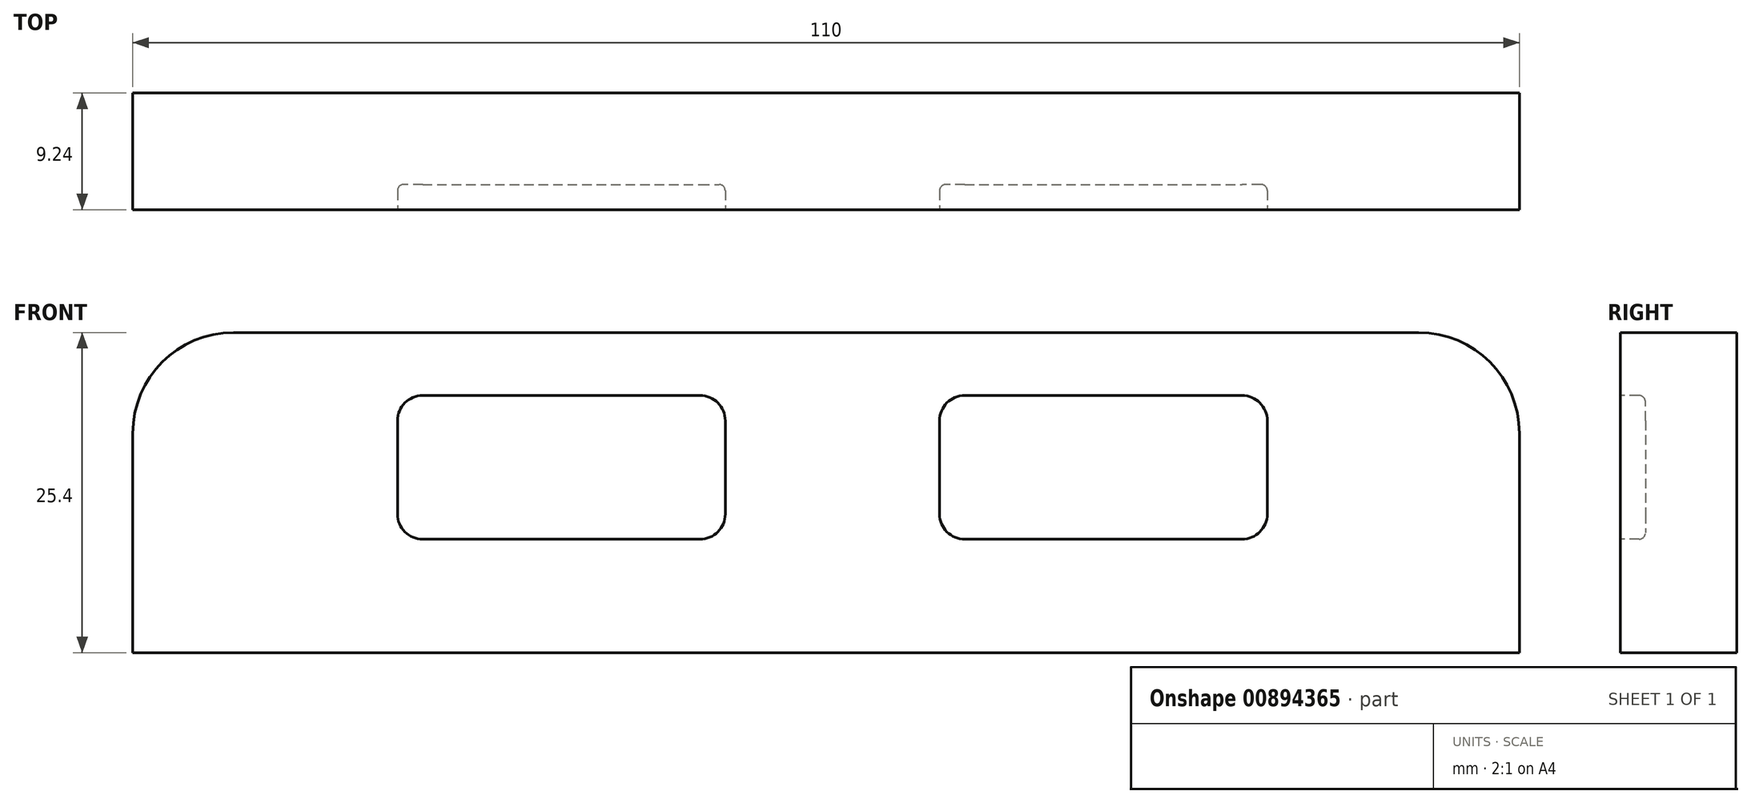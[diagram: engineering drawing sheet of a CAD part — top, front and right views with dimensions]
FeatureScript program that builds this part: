
annotation { "Feature Type Name" : "Feature", "Feature Type Description" : "" }
export const myFeature = defineFeature(function(context is Context, id is Id, definition is map)
    precondition{}
    {
        {
            var Q0;
            Q0=qCreatedBy(makeId("Front.planeOp"),FACE);
            var sketch = newSketch(context, id + "F0", { "sketchPlane" : qUnion([Q0])});
            skLineSegment(sketch, "E0.bottom", {"start": v(-1, 0) * mm, "end": v(109, 0) * mm});
            skLineSegment(sketch, "E0.top", {"start": v(-1, 25.4) * mm, "end": v(109, 25.4) * mm});
            skLineSegment(sketch, "E0.left", {"start": v(-1, 0) * mm, "end": v(-1, 25.4) * mm});
            skLineSegment(sketch, "E0.right", {"start": v(109, 0) * mm, "end": v(109, 25.4) * mm});
            skSolve(sketch);
        }
        {
            var Q0;
            Q0=makeQuery(id+"F0.imprint","IMPRINT",FACE,{"disambiguationData":[TD([[makeQuery(id+"F0.imprint","IMPRINT",EDGE,{"derivedFrom":sQuery(id+"F0.wireOp",EDGE,"E0.bottom")}),1.0]])]});
            extrude(context, id + "F1", {"entities" : qUnion([Q0]), "endBound" : BoundingType.SYMMETRIC, "depth" : 9.25 * mm, "offsetDistance" : 25 * mm});
        }
        {
            var Q0;
            Q0=makeQuery(id+"F1.opExtrude","CAP_FACE",FACE,{"disambiguationData":[OSD([sQuery(id+"F0.wireOp",EDGE,"E0.bottom"),sQuery(id+"F0.wireOp",EDGE,"E0.top"),sQuery(id+"F0.wireOp",EDGE,"E0.left"),sQuery(id+"F0.wireOp",EDGE,"E0.right")])],"isStart":false});
            var sketch = newSketch(context, id + "F2", { "sketchPlane" : qUnion([Q0])});
            skLineSegment(sketch, "E1.bottom", {"start": v(22, 9) * mm, "end": v(44, 9) * mm});
            skLineSegment(sketch, "E1.top", {"start": v(22, 20.4) * mm, "end": v(44, 20.4) * mm});
            skLineSegment(sketch, "E1.left", {"start": v(20, 11) * mm, "end": v(20, 18.4) * mm});
            skLineSegment(sketch, "E1.right", {"start": v(46, 11) * mm, "end": v(46, 18.4) * mm});
            skLineSegment(sketch, "E2.bottom", {"start": v(65, 20.4) * mm, "end": v(87, 20.4) * mm});
            skLineSegment(sketch, "E2.top", {"start": v(65, 9) * mm, "end": v(87, 9) * mm});
            skLineSegment(sketch, "E2.left", {"start": v(63, 18.4) * mm, "end": v(63, 11) * mm});
            skLineSegment(sketch, "E2.right", {"start": v(89, 18.4) * mm, "end": v(89, 11) * mm});
            skPoint(sketch, "E3.visualSharp", {"position": v(20, 20.4) * mm});
            skArc(sketch, "E3.filletArc", {"start": v(22, 20.4) * mm, "mid": v(20.59, 19.81) * mm, "end": v(20, 18.4) * mm});
            skPoint(sketch, "E4.visualSharp", {"position": v(20, 9) * mm});
            skArc(sketch, "E4.filletArc", {"start": v(20, 11) * mm, "mid": v(20.59, 9.59) * mm, "end": v(22, 9) * mm});
            skPoint(sketch, "E5.visualSharp", {"position": v(46, 9) * mm});
            skArc(sketch, "E5.filletArc", {"start": v(44, 9) * mm, "mid": v(45.41, 9.59) * mm, "end": v(46, 11) * mm});
            skPoint(sketch, "E6.visualSharp", {"position": v(46, 20.4) * mm});
            skArc(sketch, "E6.filletArc", {"start": v(46, 18.4) * mm, "mid": v(45.41, 19.81) * mm, "end": v(44, 20.4) * mm});
            skPoint(sketch, "E7.visualSharp", {"position": v(63, 20.4) * mm});
            skArc(sketch, "E7.filletArc", {"start": v(65, 20.4) * mm, "mid": v(63.59, 19.81) * mm, "end": v(63, 18.4) * mm});
            skPoint(sketch, "E8.visualSharp", {"position": v(63, 9) * mm});
            skArc(sketch, "E8.filletArc", {"start": v(63, 11) * mm, "mid": v(63.59, 9.59) * mm, "end": v(65, 9) * mm});
            skPoint(sketch, "E9.visualSharp", {"position": v(89, 9) * mm});
            skArc(sketch, "E9.filletArc", {"start": v(87, 9) * mm, "mid": v(88.41, 9.59) * mm, "end": v(89, 11) * mm});
            skPoint(sketch, "E10.visualSharp", {"position": v(89, 20.4) * mm});
            skArc(sketch, "E10.filletArc", {"start": v(89, 18.4) * mm, "mid": v(88.41, 19.81) * mm, "end": v(87, 20.4) * mm});
            skSolve(sketch);
        }
        {
            var Q0;
            Q0 = qSketchRegion(id + "F2", true);
            extrude(context, id + "F3", {"entities" : qUnion([Q0]), "operationType" : NewBodyOperationType.REMOVE, "oppositeDirection" : true, "depth" : 2 * mm, "offsetDistance" : 25 * mm});
        }
        {
            var Q0;
            Q0=makeQuery(id+"F3.boolean.opBoolean","COPY",EDGE,{"derivedFrom":makeQuery(id+"F3.opExtrude","CAP_EDGE",EDGE,{"disambiguationData":[OSD([sQuery(id+"F2.wireOp",EDGE,"E2.right")])],"isStart":false})});
            var Q1;
            Q1=makeQuery(id+"F3.boolean.opBoolean","COPY",EDGE,{"derivedFrom":makeQuery(id+"F3.opExtrude","CAP_EDGE",EDGE,{"disambiguationData":[OSD([sQuery(id+"F2.wireOp",EDGE,"E1.right")])],"isStart":false})});
            fillet(context, id + "F4", {"entities" : qUnion([Q0, Q1]), "radius" : .5 * mm, "tangentPropagation" : true, "allowEdgeOverflow" : false});
        }
        {
            var Q0;
            Q0=makeQuery(id+"F1.opExtrude","SWEPT_EDGE",EDGE,{"disambiguationData":[OSD([sQuery(id+"F0.wireOp",EDGE,"E0.top"),sQuery(id+"F0.wireOp",EDGE,"E0.right")])]});
            var Q1;
            Q1=makeQuery(id+"F1.opExtrude","SWEPT_EDGE",EDGE,{"disambiguationData":[OSD([sQuery(id+"F0.wireOp",EDGE,"E0.top"),sQuery(id+"F0.wireOp",EDGE,"E0.left")])]});
            fillet(context, id + "F5", {"entities" : qUnion([Q0, Q1]), "radius" : 8 * mm, "tangentPropagation" : true, "allowEdgeOverflow" : false});
        }
    });
